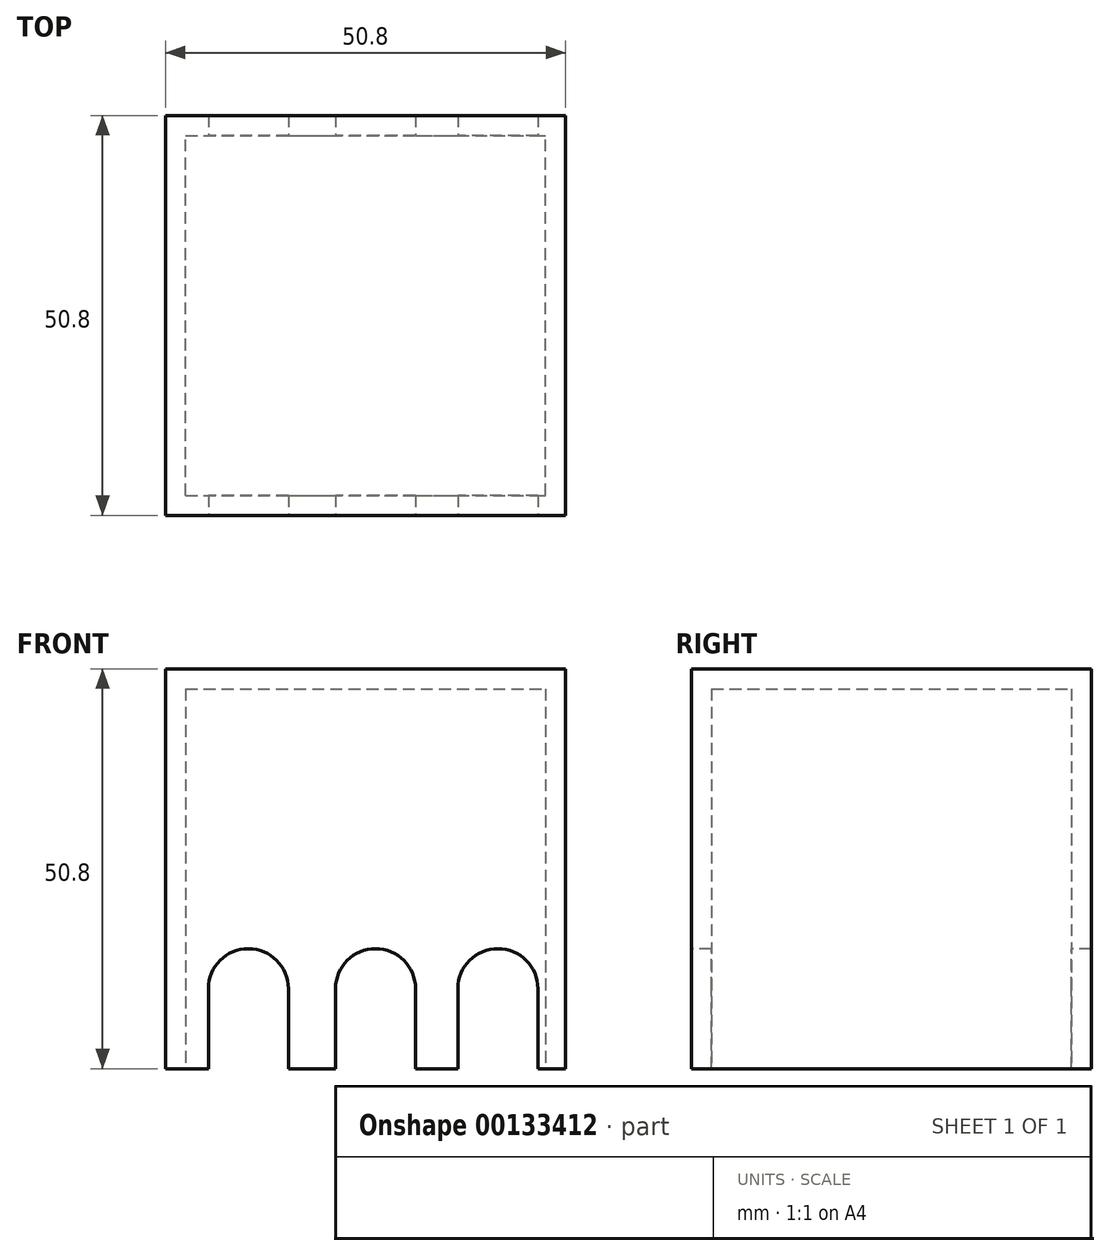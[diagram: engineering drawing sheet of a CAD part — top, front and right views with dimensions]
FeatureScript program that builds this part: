
annotation { "Feature Type Name" : "Feature", "Feature Type Description" : "" }
export const myFeature = defineFeature(function(context is Context, id is Id, definition is map)
    precondition{}
    {
        {
            var Q0;
            Q0=qCreatedBy(makeId("Front.planeOp"),FACE);
            var sketch = newSketch(context, id + "F0", { "sketchPlane" : qUnion([Q0])});
            skLineSegment(sketch, "E0.bottom", {"start": v(-25.4, 25.4) * mm, "end": v(25.4, 25.4) * mm});
            skLineSegment(sketch, "E0.top", {"start": v(-25.4, -25.4) * mm, "end": v(25.4, -25.4) * mm});
            skLineSegment(sketch, "E0.left", {"start": v(-25.4, 25.4) * mm, "end": v(-25.4, -25.4) * mm});
            skLineSegment(sketch, "E0.right", {"start": v(25.4, 25.4) * mm, "end": v(25.4, -25.4) * mm});
            skPoint(sketch, "E0.middle", {"position": v(0, 0) * mm});
            skSolve(sketch);
        }
        {
            var Q0;
            Q0 = qSketchRegion(id + "F0", true);
            extrude(context, id + "F1", {"entities" : qUnion([Q0]), "depth" : 50.8 * mm});
        }
        {
            var Q0;
            Q0=makeQuery(id+"F1.opExtrude","SWEPT_FACE",FACE,{"disambiguationData":[OSD([sQuery(id+"F0.wireOp",EDGE,"E0.top")])]});
            shell(context, id + "F2", {"entities" : qUnion([Q0]), "thickness" : 2.54 * mm});
        }
        {
            var Q0;
            Q0=makeQuery(id+"F1.opExtrude","CAP_FACE",FACE,{"disambiguationData":[OSD([sQuery(id+"F0.wireOp",EDGE,"E0.bottom"),sQuery(id+"F0.wireOp",EDGE,"E0.top"),sQuery(id+"F0.wireOp",EDGE,"E0.left"),sQuery(id+"F0.wireOp",EDGE,"E0.right")])],"isStart":false});
            var sketch = newSketch(context, id + "F3", { "sketchPlane" : qUnion([Q0])});
            skLineSegment(sketch, "E1.bottom", {"start": v(-19.96, -25.4) * mm, "end": v(-9.8, -25.4) * mm});
            skLineSegment(sketch, "E1.top", {"start": v(-19.96, -15.24) * mm, "end": v(-9.8, -15.24) * mm});
            skLineSegment(sketch, "E1.left", {"start": v(-19.96, -25.4) * mm, "end": v(-19.96, -15.24) * mm});
            skLineSegment(sketch, "E1.right", {"start": v(-9.8, -25.4) * mm, "end": v(-9.8, -15.24) * mm});
            skLineSegment(sketch, "E2.bottom", {"start": v(-3.8, -25.4) * mm, "end": v(6.35, -25.4) * mm});
            skLineSegment(sketch, "E2.top", {"start": v(-3.8, -15.24) * mm, "end": v(6.35, -15.24) * mm});
            skLineSegment(sketch, "E2.left", {"start": v(-3.8, -25.4) * mm, "end": v(-3.8, -15.24) * mm});
            skLineSegment(sketch, "E2.right", {"start": v(6.35, -25.4) * mm, "end": v(6.35, -15.24) * mm});
            skLineSegment(sketch, "E3.bottom", {"start": v(11.73, -25.4) * mm, "end": v(21.9, -25.4) * mm});
            skLineSegment(sketch, "E3.top", {"start": v(11.73, -15.24) * mm, "end": v(21.9, -15.24) * mm});
            skLineSegment(sketch, "E3.left", {"start": v(11.73, -25.4) * mm, "end": v(11.73, -15.24) * mm});
            skLineSegment(sketch, "E3.right", {"start": v(21.9, -25.4) * mm, "end": v(21.9, -15.24) * mm});
            skArc(sketch, "E4", {"start": v(-9.8, -15.24) * mm, "mid": v(-14.88, -10.16) * mm, "end": v(-19.96, -15.24) * mm});
            skArc(sketch, "E5", {"start": v(6.35, -15.24) * mm, "mid": v(1.27, -10.16) * mm, "end": v(-3.8, -15.24) * mm});
            skArc(sketch, "E6", {"start": v(21.9, -15.24) * mm, "mid": v(16.81, -10.16) * mm, "end": v(11.73, -15.24) * mm});
            skSolve(sketch);
        }
        {
            var Q0;
            Q0 = qSketchRegion(id + "F3", true);
            extrude(context, id + "F4", {"entities" : qUnion([Q0]), "operationType" : NewBodyOperationType.REMOVE, "oppositeDirection" : true, "depth" : 50.8 * mm});
        }
    });
